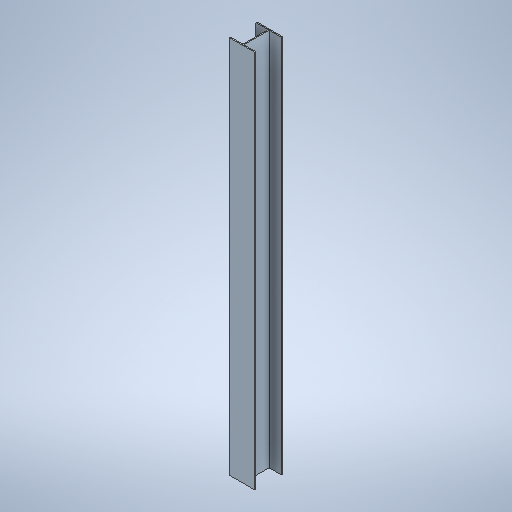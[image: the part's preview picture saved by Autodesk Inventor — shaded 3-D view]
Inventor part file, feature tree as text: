
AUTODESK INVENTOR PART (.ipt)
format: ipt  version: 2025.2 (Build 292293000, 293)  size: 261,120 bytes
history: native  units: in
note: dims shown in document units (in); Inventor stores cm internally (conversion verified against a paired STEP export)
features: other x3, plane x1, extrude x1
ambient origin geometry x8: Origin, YZ Plane, XZ Plane, XY Plane, X Axis, Y Axis, Z Axis, Center Point
bodies: Volumenkörper1 (feature_tree)
feature tree (5):
  other  "Skelett_Laufkatze.ipt"
  plane  "Arbeitsebene1"
  extrude  "Extrusion1"  Depth=0.3937in
  other  "I_Traeger_front"
  other  "I_Traeger_seite"
